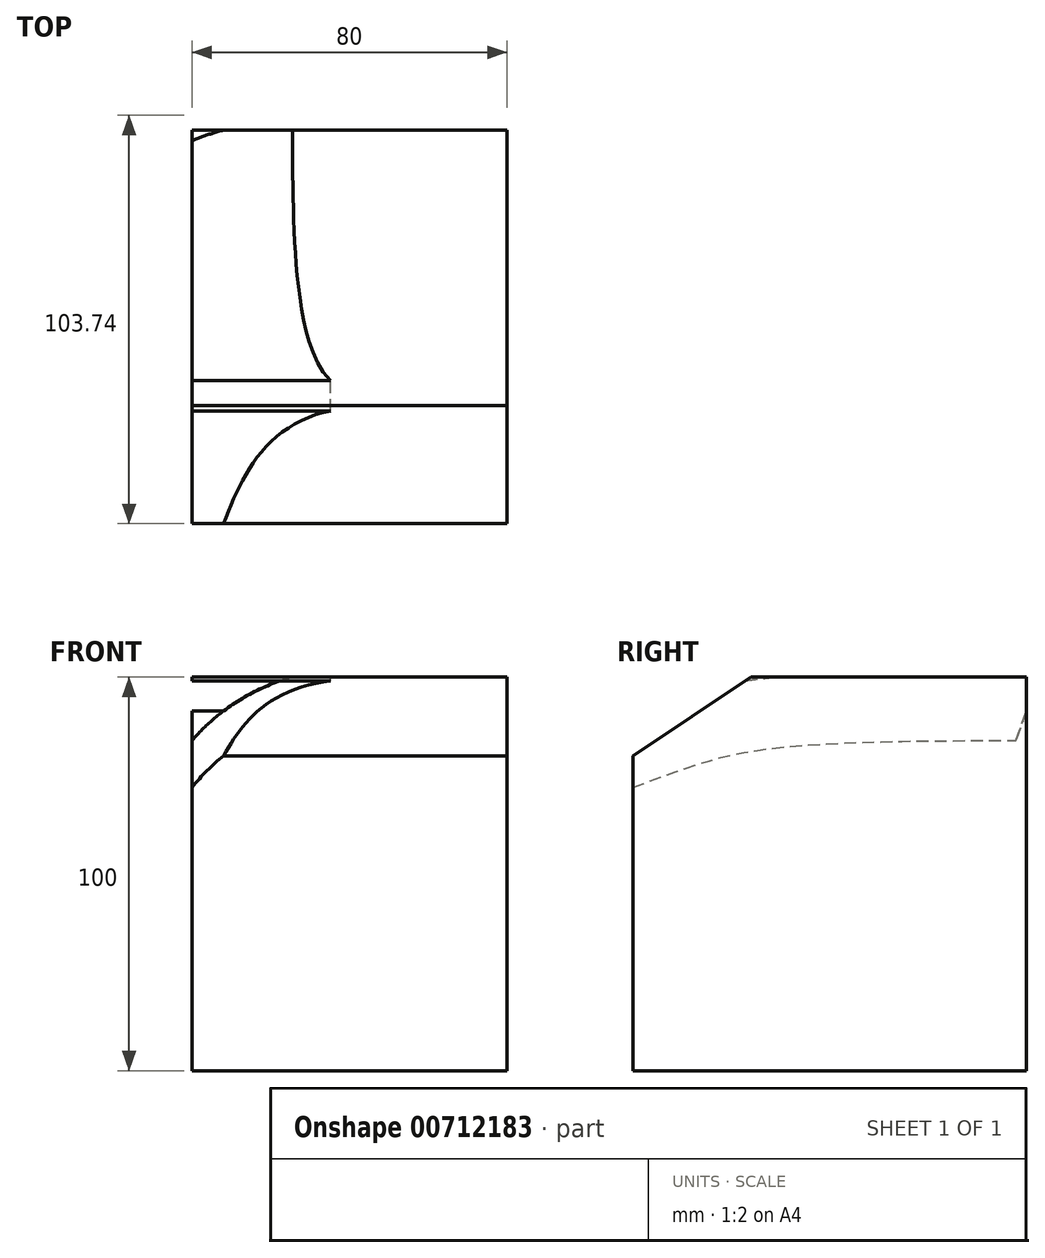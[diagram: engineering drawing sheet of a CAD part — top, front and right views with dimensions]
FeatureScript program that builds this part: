
annotation { "Feature Type Name" : "Feature", "Feature Type Description" : "" }
export const myFeature = defineFeature(function(context is Context, id is Id, definition is map)
    precondition{}
    {
        {
            var Q0;
            Q0=qCreatedBy(makeId("Front.planeOp"),FACE);
            var sketch = newSketch(context, id + "F0", { "sketchPlane" : qUnion([Q0])});
            skLineSegment(sketch, "E0.bottom", {"start": v(-40, 50) * mm, "end": v(40, 50) * mm});
            skLineSegment(sketch, "E0.top", {"start": v(-40, -50) * mm, "end": v(40, -50) * mm});
            skLineSegment(sketch, "E0.left", {"start": v(-40, 50) * mm, "end": v(-40, -50) * mm});
            skLineSegment(sketch, "E0.right", {"start": v(40, 50) * mm, "end": v(40, -50) * mm});
            skPoint(sketch, "E0.middle", {"position": v(0, 0) * mm});
            skSolve(sketch);
        }
        {
            var Q0;
            Q0 = qSketchRegion(id + "F0", true);
            extrude(context, id + "F1", {"entities" : qUnion([Q0]), "depth" : 100 * mm, "offsetDistance" : 25 * mm});
        }
        {
            var Q0;
            Q0=makeQuery(id+"F1.opExtrude","SWEPT_FACE",FACE,{"disambiguationData":[OSD([sQuery(id+"F0.wireOp",EDGE,"E0.right")])]});
            var sketch = newSketch(context, id + "F2", { "sketchPlane" : qUnion([Q0])});
            skLineSegment(sketch, "E1", {"start": v(-100, 30) * mm, "end": v(-70, 50) * mm});
            skLineSegment(sketch, "E2", {"start": v(-70, 50) * mm, "end": v(-100, 50) * mm});
            skLineSegment(sketch, "E3", {"start": v(-100, 50) * mm, "end": v(-100, 30) * mm});
            skSolve(sketch);
        }
        {
            var Q0;
            Q0 = qSketchRegion(id + "F2", true);
            extrude(context, id + "F3", {"entities" : qUnion([Q0]), "operationType" : NewBodyOperationType.REMOVE, "endBound" : BoundingType.THROUGH_ALL, "oppositeDirection" : true, "depth" : 25 * mm, "offsetDistance" : 25 * mm});
        }
        {
            var Q0;
            Q0=makeQuery(id+"F1.opExtrude","CAP_FACE",FACE,{"disambiguationData":[OSD([sQuery(id+"F0.wireOp",EDGE,"E0.bottom"),sQuery(id+"F0.wireOp",EDGE,"E0.top"),sQuery(id+"F0.wireOp",EDGE,"E0.left"),sQuery(id+"F0.wireOp",EDGE,"E0.right")])],"isStart":false});
            var sketch = newSketch(context, id + "F4", { "sketchPlane" : qUnion([Q0])});
            skLineSegment(sketch, "E4", {"start": v(0, 30) * mm, "end": v(0, -50) * mm, "construction": true});
            skArc(sketch, "E5", {"start": v(-4.8, 41) * mm, "mid": v(-24.33, 35.08) * mm, "end": v(-40, 22) * mm});
            skLineSegment(sketch, "E6", {"start": v(-40, 30) * mm, "end": v(-40, 22) * mm});
            skLineSegment(sketch, "E7", {"start": v(-40, 30) * mm, "end": v(-32, 30) * mm, "construction": true});
            skLineSegment(sketch, "E8", {"start": v(-40, 30) * mm, "end": v(-40, 41) * mm});
            skLineSegment(sketch, "E9", {"start": v(-40, 41) * mm, "end": v(-4.8, 41) * mm});
            skSolve(sketch);
        }
        {
            var Q0;
            Q0=makeQuery(id+"F1.opExtrude","SWEPT_FACE",FACE,{"disambiguationData":[OSD([sQuery(id+"F0.wireOp",EDGE,"E0.left")])]});
            var sketch = newSketch(context, id + "F5", { "sketchPlane" : qUnion([Q0])});
            skFitSpline(sketch, "E10", {"points": [v(100, 30) * mm, v(69.2, 38.87) * mm, v(0, 41.4) * mm], "startDerivative": vector(-94.5, 34.15) * mm, "endDerivative": vector(-139.91, 0) * mm});
            skSolve(sketch);
        }
        {
            var Q0;
            Q0 = qSketchRegion(id + "F4", true);
            var Q1;
            Q1=sQuery(id+"F5.wireOp",EDGE,"E10");
            sweep(context, id + "F6", {"operationType" : NewBodyOperationType.REMOVE, "profiles" : qUnion([Q0]), "path" : qUnion([Q1])});
        }
    });
